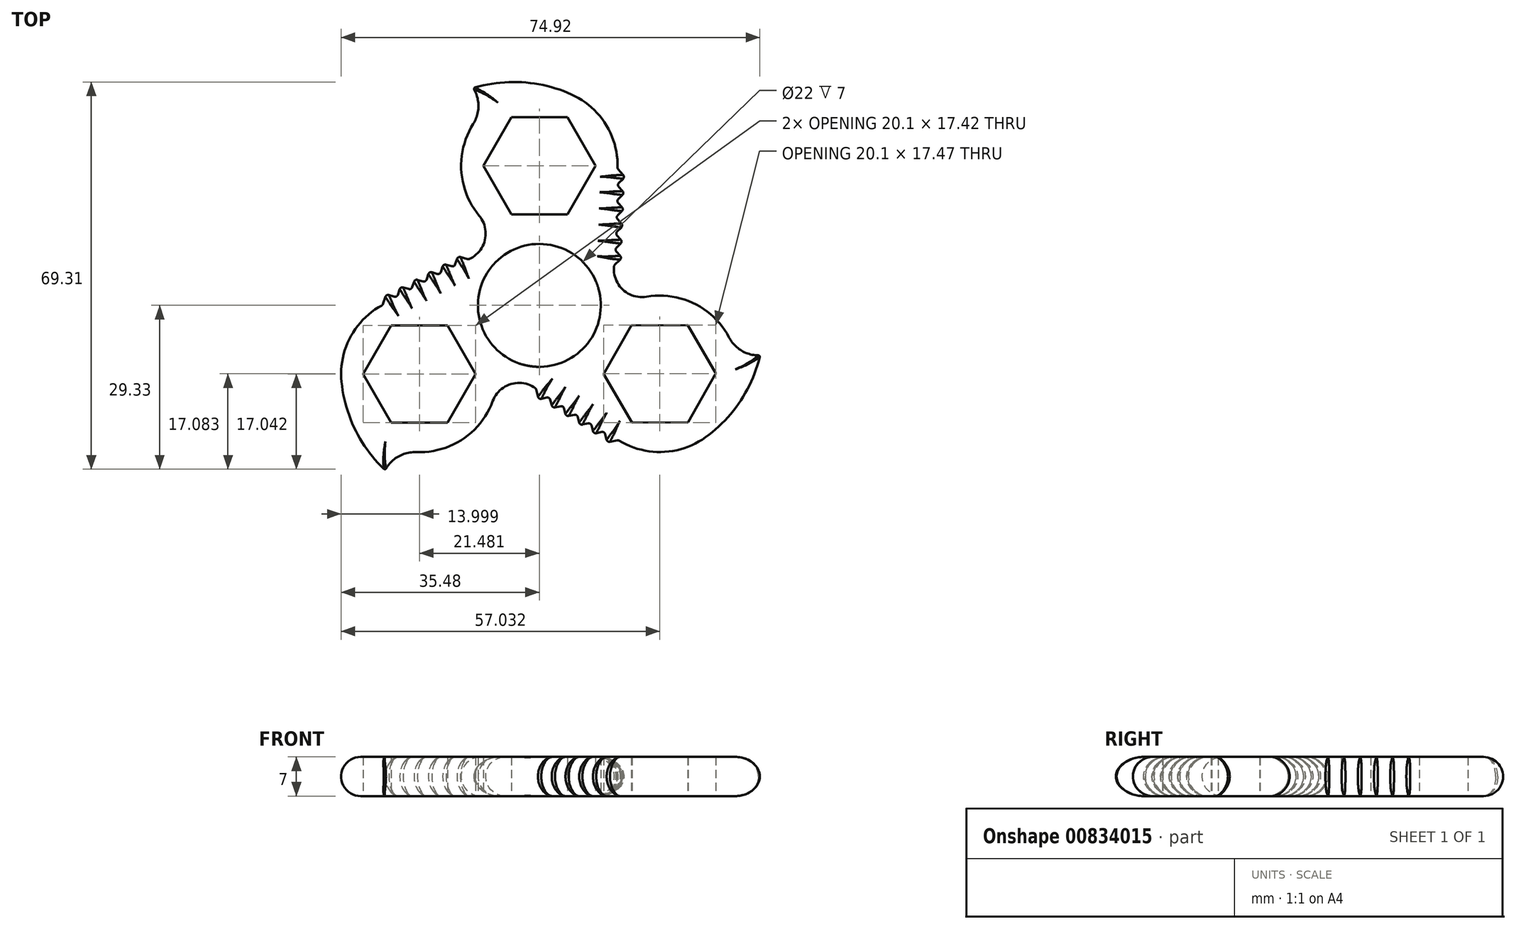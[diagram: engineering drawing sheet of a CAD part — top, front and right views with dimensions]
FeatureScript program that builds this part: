
annotation { "Feature Type Name" : "Feature", "Feature Type Description" : "" }
export const myFeature = defineFeature(function(context is Context, id is Id, definition is map)
    precondition{}
    {
        {
            var Q0;
            Q0=qCreatedBy(makeId("Top.planeOp"),FACE);
            var sketch = newSketch(context, id + "F0", { "sketchPlane" : qUnion([Q0])});
            skCircle(sketch, "E0", {"center": v(0, 0) * mm, "radius": 25 * mm, "construction": true});
            skCircle(sketch, "E1", {"center": v(0, 0) * mm, "radius": 11 * mm});
            skPoint(sketch, "E2.center", {"position": v(13.99, -7.94) * mm});
            skArc(sketch, "E3", {"start": v(14, 24.5) * mm, "mid": v(11.9, 32.39) * mm, "end": v(5.75, 37.77) * mm});
            skLineSegment(sketch, "E4", {"start": v(13.35, 6.66) * mm, "end": v(13.36, 7.1) * mm});
            skPoint(sketch, "E5.visualSharp", {"position": v(-4.7, 11.81) * mm});
            skArc(sketch, "E5.filletArc", {"start": v(-12.27, 8.44) * mm, "mid": v(-9.7, 11.89) * mm, "end": v(-10.77, 16.05) * mm});
            skPoint(sketch, "E6.visualSharp", {"position": v(13.05, -1.63) * mm});
            skArc(sketch, "E7", {"start": v(5.75, 37.77) * mm, "mid": v(-2.94, 39.93) * mm, "end": v(-11.83, 38.9) * mm});
            skArc(sketch, "E8", {"start": v(-11.83, 32.48) * mm, "mid": v(-10.9, 35.7) * mm, "end": v(-11.83, 38.9) * mm});
            skArc(sketch, "E9.trimOffspring", {"start": v(-11.83, 32.48) * mm, "mid": v(-13.97, 24.1) * mm, "end": v(-10.77, 16.05) * mm});
            skLineSegment(sketch, "E10", {"start": v(14, 24.5) * mm, "end": v(15.31, 23) * mm});
            skLineSegment(sketch, "E11", {"start": v(15.31, 23) * mm, "end": v(13.89, 21.6) * mm});
            skLineSegment(sketch, "E12.1.0.0", {"start": v(15.2, 20.1) * mm, "end": v(13.78, 18.7) * mm});
            skLineSegment(sketch, "E12.1.0.1", {"start": v(13.89, 21.6) * mm, "end": v(15.2, 20.1) * mm});
            skLineSegment(sketch, "E12.2.0.0", {"start": v(15.1, 17.2) * mm, "end": v(13.68, 15.8) * mm});
            skLineSegment(sketch, "E12.2.0.1", {"start": v(13.78, 18.7) * mm, "end": v(15.1, 17.2) * mm});
            skLineSegment(sketch, "E12.3.0.0", {"start": v(15, 14.3) * mm, "end": v(13.57, 12.9) * mm});
            skLineSegment(sketch, "E12.3.0.1", {"start": v(13.68, 15.8) * mm, "end": v(15, 14.3) * mm});
            skLineSegment(sketch, "E12.4.0.0", {"start": v(14.9, 11.4) * mm, "end": v(13.47, 10) * mm});
            skLineSegment(sketch, "E12.4.0.1", {"start": v(13.57, 12.9) * mm, "end": v(14.9, 11.4) * mm});
            skLineSegment(sketch, "E12.5.0.0", {"start": v(14.79, 8.5) * mm, "end": v(13.36, 7.1) * mm});
            skLineSegment(sketch, "E12.5.0.1", {"start": v(13.47, 10) * mm, "end": v(14.79, 8.5) * mm});
            skArc(sketch, "E13.1.0", {"start": v(-22.04, -26.28) * mm, "mid": v(-25.29, -27.08) * mm, "end": v(-27.6, -29.49) * mm});
            skArc(sketch, "E13.1.1", {"start": v(-1, -14.64) * mm, "mid": v(-5.27, -14.14) * mm, "end": v(-8.35, -17.14) * mm});
            skArc(sketch, "E13.1.2", {"start": v(-22.04, -26.28) * mm, "mid": v(-13.71, -23.93) * mm, "end": v(-8.35, -17.14) * mm});
            skArc(sketch, "E13.1.3", {"start": v(-35.41, -13.7) * mm, "mid": v(-32.94, -22.3) * mm, "end": v(-27.6, -29.49) * mm});
            skArc(sketch, "E13.1.4", {"start": v(-28.04, 0.08) * mm, "mid": v(-33.82, -5.68) * mm, "end": v(-35.41, -13.7) * mm});
            skLineSegment(sketch, "E13.1.6", {"start": v(-28.04, 0.08) * mm, "end": v(-27.4, 1.98) * mm});
            skLineSegment(sketch, "E13.1.7", {"start": v(-27.4, 1.98) * mm, "end": v(-25.47, 1.44) * mm});
            skLineSegment(sketch, "E13.1.8", {"start": v(-25.48, 1.44) * mm, "end": v(-24.84, 3.34) * mm});
            skLineSegment(sketch, "E13.1.9", {"start": v(-24.84, 3.34) * mm, "end": v(-22.91, 2.8) * mm});
            skLineSegment(sketch, "E13.1.10", {"start": v(-22.91, 2.8) * mm, "end": v(-22.28, 4.7) * mm});
            skLineSegment(sketch, "E13.1.11", {"start": v(-22.28, 4.7) * mm, "end": v(-20.35, 4.16) * mm});
            skLineSegment(sketch, "E13.1.12", {"start": v(-20.35, 4.16) * mm, "end": v(-19.71, 6.05) * mm});
            skLineSegment(sketch, "E13.1.13", {"start": v(-19.71, 6.05) * mm, "end": v(-17.79, 5.52) * mm});
            skLineSegment(sketch, "E13.1.14", {"start": v(-17.79, 5.51) * mm, "end": v(-17.15, 7.41) * mm});
            skLineSegment(sketch, "E13.1.15", {"start": v(-17.15, 7.41) * mm, "end": v(-15.23, 6.87) * mm});
            skLineSegment(sketch, "E13.1.16", {"start": v(-15.23, 6.87) * mm, "end": v(-14.59, 8.77) * mm});
            skLineSegment(sketch, "E13.1.17", {"start": v(-14.59, 8.77) * mm, "end": v(-12.66, 8.23) * mm});
            skLineSegment(sketch, "E13.1.18", {"start": v(-12.27, 8.44) * mm, "end": v(-12.66, 8.23) * mm});
            skArc(sketch, "E13.2.0", {"start": v(33.95, -5.74) * mm, "mid": v(36.26, -8.15) * mm, "end": v(39.5, -8.95) * mm});
            skArc(sketch, "E13.2.1", {"start": v(13.35, 6.66) * mm, "mid": v(15.05, 2.72) * mm, "end": v(19.19, 1.55) * mm});
            skArc(sketch, "E13.2.2", {"start": v(33.95, -5.74) * mm, "mid": v(27.75, 0.3) * mm, "end": v(19.19, 1.55) * mm});
            skArc(sketch, "E13.2.3", {"start": v(29.73, -23.6) * mm, "mid": v(35.95, -17.16) * mm, "end": v(39.5, -8.95) * mm});
            skArc(sketch, "E13.2.4", {"start": v(14.12, -24.11) * mm, "mid": v(22, -26.24) * mm, "end": v(29.73, -23.6) * mm});
            skLineSegment(sketch, "E13.2.6", {"start": v(14.12, -24.11) * mm, "end": v(12.16, -24.5) * mm});
            skLineSegment(sketch, "E13.2.7", {"start": v(12.16, -24.5) * mm, "end": v(11.66, -22.57) * mm});
            skLineSegment(sketch, "E13.2.8", {"start": v(11.66, -22.57) * mm, "end": v(9.7, -22.97) * mm});
            skLineSegment(sketch, "E13.2.9", {"start": v(9.7, -22.97) * mm, "end": v(9.2, -21.03) * mm});
            skLineSegment(sketch, "E13.2.10", {"start": v(9.2, -21.03) * mm, "end": v(7.24, -21.43) * mm});
            skLineSegment(sketch, "E13.2.11", {"start": v(7.24, -21.43) * mm, "end": v(6.74, -19.5) * mm});
            skLineSegment(sketch, "E13.2.12", {"start": v(6.75, -19.5) * mm, "end": v(4.79, -19.89) * mm});
            skLineSegment(sketch, "E13.2.13", {"start": v(4.79, -19.89) * mm, "end": v(4.29, -17.95) * mm});
            skLineSegment(sketch, "E13.2.14", {"start": v(4.29, -17.95) * mm, "end": v(2.33, -18.35) * mm});
            skLineSegment(sketch, "E13.2.15", {"start": v(2.33, -18.35) * mm, "end": v(1.83, -16.41) * mm});
            skLineSegment(sketch, "E13.2.16", {"start": v(1.83, -16.41) * mm, "end": v(-0.13, -16.8) * mm});
            skLineSegment(sketch, "E13.2.17", {"start": v(-0.13, -16.8) * mm, "end": v(-0.63, -14.87) * mm});
            skLineSegment(sketch, "E13.2.18", {"start": v(-1, -14.64) * mm, "end": v(-0.63, -14.87) * mm});
            skPoint(sketch, "E13.center", {"position": v(0.03, -3.97) * mm});
            skLineSegment(sketch, "E14.trimOffspring", {"start": v(-25.47, 1.44) * mm, "end": v(-25.48, 1.44) * mm});
            skLineSegment(sketch, "E15.trimOffspring", {"start": v(-22.91, 2.8) * mm, "end": v(-22.91, 2.8) * mm});
            skLineSegment(sketch, "E16.trimOffspring", {"start": v(-20.35, 4.16) * mm, "end": v(-20.35, 4.16) * mm});
            skLineSegment(sketch, "E17.trimOffspring", {"start": v(-17.79, 5.52) * mm, "end": v(-17.79, 5.51) * mm});
            skLineSegment(sketch, "E18.trimOffspring", {"start": v(-15.23, 6.87) * mm, "end": v(-15.23, 6.87) * mm});
            skLineSegment(sketch, "E19.trimOffspring", {"start": v(1.83, -16.41) * mm, "end": v(1.83, -16.41) * mm});
            skLineSegment(sketch, "E20.trimOffspring", {"start": v(4.29, -17.95) * mm, "end": v(4.29, -17.95) * mm});
            skLineSegment(sketch, "E21.trimOffspring", {"start": v(6.74, -19.5) * mm, "end": v(6.75, -19.5) * mm});
            skLineSegment(sketch, "E22.trimOffspring", {"start": v(9.2, -21.03) * mm, "end": v(9.2, -21.03) * mm});
            skLineSegment(sketch, "E23.trimOffspring", {"start": v(11.26, -22.32) * mm, "end": v(11.66, -22.57) * mm});
            skLineSegment(sketch, "E24.trimOffspring", {"start": v(13.47, 10) * mm, "end": v(13.47, 10) * mm});
            skLineSegment(sketch, "E25.trimOffspring", {"start": v(13.57, 12.9) * mm, "end": v(13.57, 12.9) * mm});
            skLineSegment(sketch, "E26.trimOffspring", {"start": v(13.68, 15.8) * mm, "end": v(13.68, 15.8) * mm});
            skLineSegment(sketch, "E27.trimOffspring", {"start": v(13.78, 18.7) * mm, "end": v(13.78, 18.7) * mm});
            skLineSegment(sketch, "E28.trimOffspring", {"start": v(13.78, 18.7) * mm, "end": v(13.78, 18.7) * mm, "construction": true});
            skLineSegment(sketch, "E29.trimOffspring", {"start": v(13.89, 21.6) * mm, "end": v(13.89, 21.6) * mm});
            skPoint(sketch, "E30.0.midPoint", {"position": v(0, 33.7) * mm});
            skLineSegment(sketch, "E31.0", {"start": v(11.5, -12.3) * mm, "end": v(16.47, -3.57) * mm});
            skLineSegment(sketch, "E31.1", {"start": v(16.47, -3.57) * mm, "end": v(26.53, -3.51) * mm});
            skLineSegment(sketch, "E31.2", {"start": v(26.53, -3.51) * mm, "end": v(31.6, -12.19) * mm});
            skLineSegment(sketch, "E31.3", {"start": v(31.6, -12.19) * mm, "end": v(26.63, -20.92) * mm});
            skLineSegment(sketch, "E31.4", {"start": v(26.63, -20.92) * mm, "end": v(16.58, -20.98) * mm});
            skLineSegment(sketch, "E31.5", {"start": v(16.58, -20.98) * mm, "end": v(11.5, -12.3) * mm});
            skCircle(sketch, "E32.cCircle", {"center": v(-21.48, -12.29) * mm, "radius": 8.7 * mm, "construction": true});
            skLineSegment(sketch, "E32.0", {"start": v(-16.46, -3.58) * mm, "end": v(-11.43, -12.28) * mm});
            skLineSegment(sketch, "E32.1", {"start": v(-11.43, -12.28) * mm, "end": v(-16.45, -20.99) * mm});
            skLineSegment(sketch, "E32.2", {"start": v(-16.45, -20.99) * mm, "end": v(-26.5, -21) * mm});
            skLineSegment(sketch, "E32.3", {"start": v(-26.5, -21) * mm, "end": v(-31.53, -12.3) * mm});
            skLineSegment(sketch, "E32.4", {"start": v(-31.53, -12.3) * mm, "end": v(-26.52, -3.59) * mm});
            skLineSegment(sketch, "E32.5", {"start": v(-26.52, -3.59) * mm, "end": v(-16.46, -3.58) * mm});
            skPoint(sketch, "E32.0.midPoint", {"position": v(-13.95, -7.93) * mm});
            skLineSegment(sketch, "E33", {"start": v(0.03, -3.97) * mm, "end": v(0, 25) * mm});
            skCircle(sketch, "E34.cCircle", {"center": v(0, 25) * mm, "radius": 8.7 * mm, "construction": true});
            skLineSegment(sketch, "E34.0", {"start": v(5.03, 16.3) * mm, "end": v(-5.02, 16.3) * mm});
            skLineSegment(sketch, "E34.1", {"start": v(-5.02, 16.3) * mm, "end": v(-10.05, 25) * mm});
            skLineSegment(sketch, "E34.2", {"start": v(-10.05, 25) * mm, "end": v(-5.03, 33.7) * mm});
            skLineSegment(sketch, "E34.3", {"start": v(-5.03, 33.7) * mm, "end": v(5.02, 33.7) * mm});
            skLineSegment(sketch, "E34.4", {"start": v(5.02, 33.7) * mm, "end": v(10.05, 25) * mm});
            skLineSegment(sketch, "E34.5", {"start": v(10.05, 25) * mm, "end": v(5.03, 16.3) * mm});
            skPoint(sketch, "E34.0.midPoint", {"position": v(0, 16.3) * mm});
            skSolve(sketch);
        }
        {
            var Q0;
            Q0=qSketchRegion(id+"F0",true);
            extrude(context, id + "F1", {"entities" : qUnion([Q0]), "depth" : 7 * mm, "offsetDistance" : 25 * mm});
        }
        {
            var Q0;
            Q0=makeQuery(id+"F1.opExtrude","SWEPT_EDGE",EDGE,{"disambiguationData":[OSD([sQuery(id+"F0.wireOp",EDGE,"E13.1.17"),sQuery(id+"F0.wireOp",EDGE,"E13.1.18")])]});
            var Q1;
            Q1=makeQuery(id+"F1.opExtrude","SWEPT_EDGE",EDGE,{"disambiguationData":[OSD([sQuery(id+"F0.wireOp",EDGE,"E13.1.16"),sQuery(id+"F0.wireOp",EDGE,"E13.1.17")])]});
            var Q2;
            Q2=makeQuery(id+"F1.opExtrude","SWEPT_EDGE",EDGE,{"disambiguationData":[OSD([sQuery(id+"F0.wireOp",EDGE,"E13.1.15"),sQuery(id+"F0.wireOp",EDGE,"E13.1.16")])]});
            var Q3;
            Q3=makeQuery(id+"F1.opExtrude","SWEPT_EDGE",EDGE,{"disambiguationData":[OSD([sQuery(id+"F0.wireOp",EDGE,"E13.1.14"),sQuery(id+"F0.wireOp",EDGE,"E13.1.15")])]});
            var Q4;
            Q4=makeQuery(id+"F1.opExtrude","SWEPT_EDGE",EDGE,{"disambiguationData":[OSD([sQuery(id+"F0.wireOp",EDGE,"E13.1.13"),sQuery(id+"F0.wireOp",EDGE,"E13.1.14")])]});
            var Q5;
            Q5=makeQuery(id+"F1.opExtrude","SWEPT_EDGE",EDGE,{"disambiguationData":[OSD([sQuery(id+"F0.wireOp",EDGE,"E13.1.12"),sQuery(id+"F0.wireOp",EDGE,"E13.1.13")])]});
            var Q6;
            Q6=makeQuery(id+"F1.opExtrude","SWEPT_EDGE",EDGE,{"disambiguationData":[OSD([sQuery(id+"F0.wireOp",EDGE,"E13.1.11"),sQuery(id+"F0.wireOp",EDGE,"E13.1.12")])]});
            var Q7;
            Q7=makeQuery(id+"F1.opExtrude","SWEPT_EDGE",EDGE,{"disambiguationData":[OSD([sQuery(id+"F0.wireOp",EDGE,"E13.1.10"),sQuery(id+"F0.wireOp",EDGE,"E13.1.11")])]});
            var Q8;
            Q8=makeQuery(id+"F1.opExtrude","SWEPT_EDGE",EDGE,{"disambiguationData":[OSD([sQuery(id+"F0.wireOp",EDGE,"E13.1.9"),sQuery(id+"F0.wireOp",EDGE,"E13.1.10")])]});
            var Q9;
            Q9=makeQuery(id+"F1.opExtrude","SWEPT_EDGE",EDGE,{"disambiguationData":[OSD([sQuery(id+"F0.wireOp",EDGE,"E13.1.8"),sQuery(id+"F0.wireOp",EDGE,"E13.1.9")])]});
            var Q10;
            Q10=makeQuery(id+"F1.opExtrude","SWEPT_EDGE",EDGE,{"disambiguationData":[OSD([sQuery(id+"F0.wireOp",EDGE,"E13.1.7"),sQuery(id+"F0.wireOp",EDGE,"E13.1.8")])]});
            var Q11;
            Q11=makeQuery(id+"F1.opExtrude","SWEPT_EDGE",EDGE,{"disambiguationData":[OSD([sQuery(id+"F0.wireOp",EDGE,"E13.1.6"),sQuery(id+"F0.wireOp",EDGE,"E13.1.7")])]});
            var Q12;
            Q12=makeQuery(id+"F1.opExtrude","SWEPT_EDGE",EDGE,{"disambiguationData":[OSD([sQuery(id+"F0.wireOp",EDGE,"E13.1.4"),sQuery(id+"F0.wireOp",EDGE,"E13.1.6")])]});
            var Q13;
            Q13=makeQuery(id+"F1.opExtrude","SWEPT_EDGE",EDGE,{"disambiguationData":[OSD([sQuery(id+"F0.wireOp",EDGE,"E13.2.17"),sQuery(id+"F0.wireOp",EDGE,"E13.2.18")])]});
            var Q14;
            Q14=makeQuery(id+"F1.opExtrude","SWEPT_EDGE",EDGE,{"disambiguationData":[OSD([sQuery(id+"F0.wireOp",EDGE,"E13.2.16"),sQuery(id+"F0.wireOp",EDGE,"E13.2.17")])]});
            var Q15;
            Q15=makeQuery(id+"F1.opExtrude","SWEPT_EDGE",EDGE,{"disambiguationData":[OSD([sQuery(id+"F0.wireOp",EDGE,"E13.2.15"),sQuery(id+"F0.wireOp",EDGE,"E13.2.16")])]});
            var Q16;
            Q16=makeQuery(id+"F1.opExtrude","SWEPT_EDGE",EDGE,{"disambiguationData":[OSD([sQuery(id+"F0.wireOp",EDGE,"E13.2.14"),sQuery(id+"F0.wireOp",EDGE,"E13.2.15")])]});
            var Q17;
            Q17=makeQuery(id+"F1.opExtrude","SWEPT_EDGE",EDGE,{"disambiguationData":[OSD([sQuery(id+"F0.wireOp",EDGE,"E13.2.13"),sQuery(id+"F0.wireOp",EDGE,"E13.2.14")])]});
            var Q18;
            Q18=makeQuery(id+"F1.opExtrude","SWEPT_EDGE",EDGE,{"disambiguationData":[OSD([sQuery(id+"F0.wireOp",EDGE,"E13.2.12"),sQuery(id+"F0.wireOp",EDGE,"E13.2.13")])]});
            var Q19;
            Q19=makeQuery(id+"F1.opExtrude","SWEPT_EDGE",EDGE,{"disambiguationData":[OSD([sQuery(id+"F0.wireOp",EDGE,"E13.2.11"),sQuery(id+"F0.wireOp",EDGE,"E13.2.12")])]});
            var Q20;
            Q20=makeQuery(id+"F1.opExtrude","SWEPT_EDGE",EDGE,{"disambiguationData":[OSD([sQuery(id+"F0.wireOp",EDGE,"E13.2.10"),sQuery(id+"F0.wireOp",EDGE,"E13.2.11")])]});
            var Q21;
            Q21=makeQuery(id+"F1.opExtrude","SWEPT_EDGE",EDGE,{"disambiguationData":[OSD([sQuery(id+"F0.wireOp",EDGE,"E13.2.9"),sQuery(id+"F0.wireOp",EDGE,"E13.2.10")])]});
            var Q22;
            Q22=makeQuery(id+"F1.opExtrude","SWEPT_EDGE",EDGE,{"disambiguationData":[OSD([sQuery(id+"F0.wireOp",EDGE,"E13.2.8"),sQuery(id+"F0.wireOp",EDGE,"E13.2.9")])]});
            var Q23;
            Q23=makeQuery(id+"F1.opExtrude","SWEPT_EDGE",EDGE,{"disambiguationData":[OSD([sQuery(id+"F0.wireOp",EDGE,"E13.2.7"),sQuery(id+"F0.wireOp",EDGE,"E13.2.8")])]});
            var Q24;
            Q24=makeQuery(id+"F1.opExtrude","SWEPT_EDGE",EDGE,{"disambiguationData":[OSD([sQuery(id+"F0.wireOp",EDGE,"E13.2.6"),sQuery(id+"F0.wireOp",EDGE,"E13.2.7")])]});
            var Q25;
            Q25=makeQuery(id+"F1.opExtrude","SWEPT_EDGE",EDGE,{"disambiguationData":[OSD([sQuery(id+"F0.wireOp",EDGE,"E13.2.4"),sQuery(id+"F0.wireOp",EDGE,"E13.2.6")])]});
            var Q26;
            Q26=makeQuery(id+"F1.opExtrude","SWEPT_EDGE",EDGE,{"disambiguationData":[OSD([sQuery(id+"F0.wireOp",EDGE,"E3"),sQuery(id+"F0.wireOp",EDGE,"E10")])]});
            var Q27;
            Q27=makeQuery(id+"F1.opExtrude","SWEPT_EDGE",EDGE,{"disambiguationData":[OSD([sQuery(id+"F0.wireOp",EDGE,"E10"),sQuery(id+"F0.wireOp",EDGE,"E11")])]});
            var Q28;
            Q28=makeQuery(id+"F1.opExtrude","SWEPT_EDGE",EDGE,{"disambiguationData":[OSD([sQuery(id+"F0.wireOp",EDGE,"E11"),sQuery(id+"F0.wireOp",EDGE,"E12.1.0.1")])]});
            var Q29;
            Q29=makeQuery(id+"F1.opExtrude","SWEPT_EDGE",EDGE,{"disambiguationData":[OSD([sQuery(id+"F0.wireOp",EDGE,"E12.1.0.0"),sQuery(id+"F0.wireOp",EDGE,"E12.1.0.1")])]});
            var Q30;
            Q30=makeQuery(id+"F1.opExtrude","SWEPT_EDGE",EDGE,{"disambiguationData":[OSD([sQuery(id+"F0.wireOp",EDGE,"E12.1.0.0"),sQuery(id+"F0.wireOp",EDGE,"E12.2.0.1")])]});
            var Q31;
            Q31=makeQuery(id+"F1.opExtrude","SWEPT_EDGE",EDGE,{"disambiguationData":[OSD([sQuery(id+"F0.wireOp",EDGE,"E12.2.0.0"),sQuery(id+"F0.wireOp",EDGE,"E12.2.0.1")])]});
            var Q32;
            Q32=makeQuery(id+"F1.opExtrude","SWEPT_EDGE",EDGE,{"disambiguationData":[OSD([sQuery(id+"F0.wireOp",EDGE,"E12.2.0.0"),sQuery(id+"F0.wireOp",EDGE,"E12.3.0.1")])]});
            var Q33;
            Q33=makeQuery(id+"F1.opExtrude","SWEPT_EDGE",EDGE,{"disambiguationData":[OSD([sQuery(id+"F0.wireOp",EDGE,"E12.3.0.0"),sQuery(id+"F0.wireOp",EDGE,"E12.3.0.1")])]});
            var Q34;
            Q34=makeQuery(id+"F1.opExtrude","SWEPT_EDGE",EDGE,{"disambiguationData":[OSD([sQuery(id+"F0.wireOp",EDGE,"E12.3.0.0"),sQuery(id+"F0.wireOp",EDGE,"E12.4.0.1")])]});
            var Q35;
            Q35=makeQuery(id+"F1.opExtrude","SWEPT_EDGE",EDGE,{"disambiguationData":[OSD([sQuery(id+"F0.wireOp",EDGE,"E12.4.0.0"),sQuery(id+"F0.wireOp",EDGE,"E12.4.0.1")])]});
            var Q36;
            Q36=makeQuery(id+"F1.opExtrude","SWEPT_EDGE",EDGE,{"disambiguationData":[OSD([sQuery(id+"F0.wireOp",EDGE,"E12.4.0.0"),sQuery(id+"F0.wireOp",EDGE,"E12.5.0.1")])]});
            var Q37;
            Q37=makeQuery(id+"F1.opExtrude","SWEPT_EDGE",EDGE,{"disambiguationData":[OSD([sQuery(id+"F0.wireOp",EDGE,"E12.5.0.0"),sQuery(id+"F0.wireOp",EDGE,"E12.5.0.1")])]});
            var Q38;
            Q38=makeQuery(id+"F1.opExtrude","SWEPT_EDGE",EDGE,{"disambiguationData":[OSD([sQuery(id+"F0.wireOp",EDGE,"E4"),sQuery(id+"F0.wireOp",EDGE,"E12.5.0.0")])]});
            fillet(context, id + "F2", {"entities" : qUnion([Q0, Q1, Q2, Q3, Q4, Q5, Q6, Q7, Q8, Q9, Q10, Q11, Q12, Q13, Q14, Q15, Q16, Q17, Q18, Q19, Q20, Q21, Q22, Q23, Q24, Q25, Q26, Q27, Q28, Q29, Q30, Q31, Q32, Q33, Q34, Q35, Q36, Q37, Q38]), "radius" : .5 * mm, "tangentPropagation" : true, "allowEdgeOverflow" : false});
        }
        {
            var Q0;
            Q0=makeQuery(id+"F1.opExtrude","SWEPT_EDGE",EDGE,{"disambiguationData":[OSD([sQuery(id+"F0.wireOp",EDGE,"E7"),sQuery(id+"F0.wireOp",EDGE,"E8")])]});
            var Q1;
            Q1=makeQuery(id+"F1.opExtrude","SWEPT_EDGE",EDGE,{"disambiguationData":[OSD([sQuery(id+"F0.wireOp",EDGE,"E13.1.0"),sQuery(id+"F0.wireOp",EDGE,"E13.1.3")])]});
            var Q2;
            Q2=makeQuery(id+"F1.opExtrude","SWEPT_EDGE",EDGE,{"disambiguationData":[OSD([sQuery(id+"F0.wireOp",EDGE,"E13.2.0"),sQuery(id+"F0.wireOp",EDGE,"E13.2.3")])]});
            fillet(context, id + "F3", {"entities" : qUnion([Q0, Q1, Q2]), "radius" : .25 * mm, "tangentPropagation" : true, "allowEdgeOverflow" : false});
        }
        {
            var Q0;
            Q0=makeQuery(id+"F1.opExtrude","CAP_EDGE",EDGE,{"disambiguationData":[OSD([sQuery(id+"F0.wireOp",EDGE,"E13.2.4")])],"isStart":false});
            var Q1;
            Q1=makeQuery(id+"F1.opExtrude","CAP_EDGE",EDGE,{"disambiguationData":[OSD([sQuery(id+"F0.wireOp",EDGE,"E13.1.1")])],"isStart":true});
            fillet(context, id + "F4", {"entities" : qUnion([Q0, Q1]), "radius" : 3.5 * mm, "tangentPropagation" : true, "allowEdgeOverflow" : false});
        }
    });
